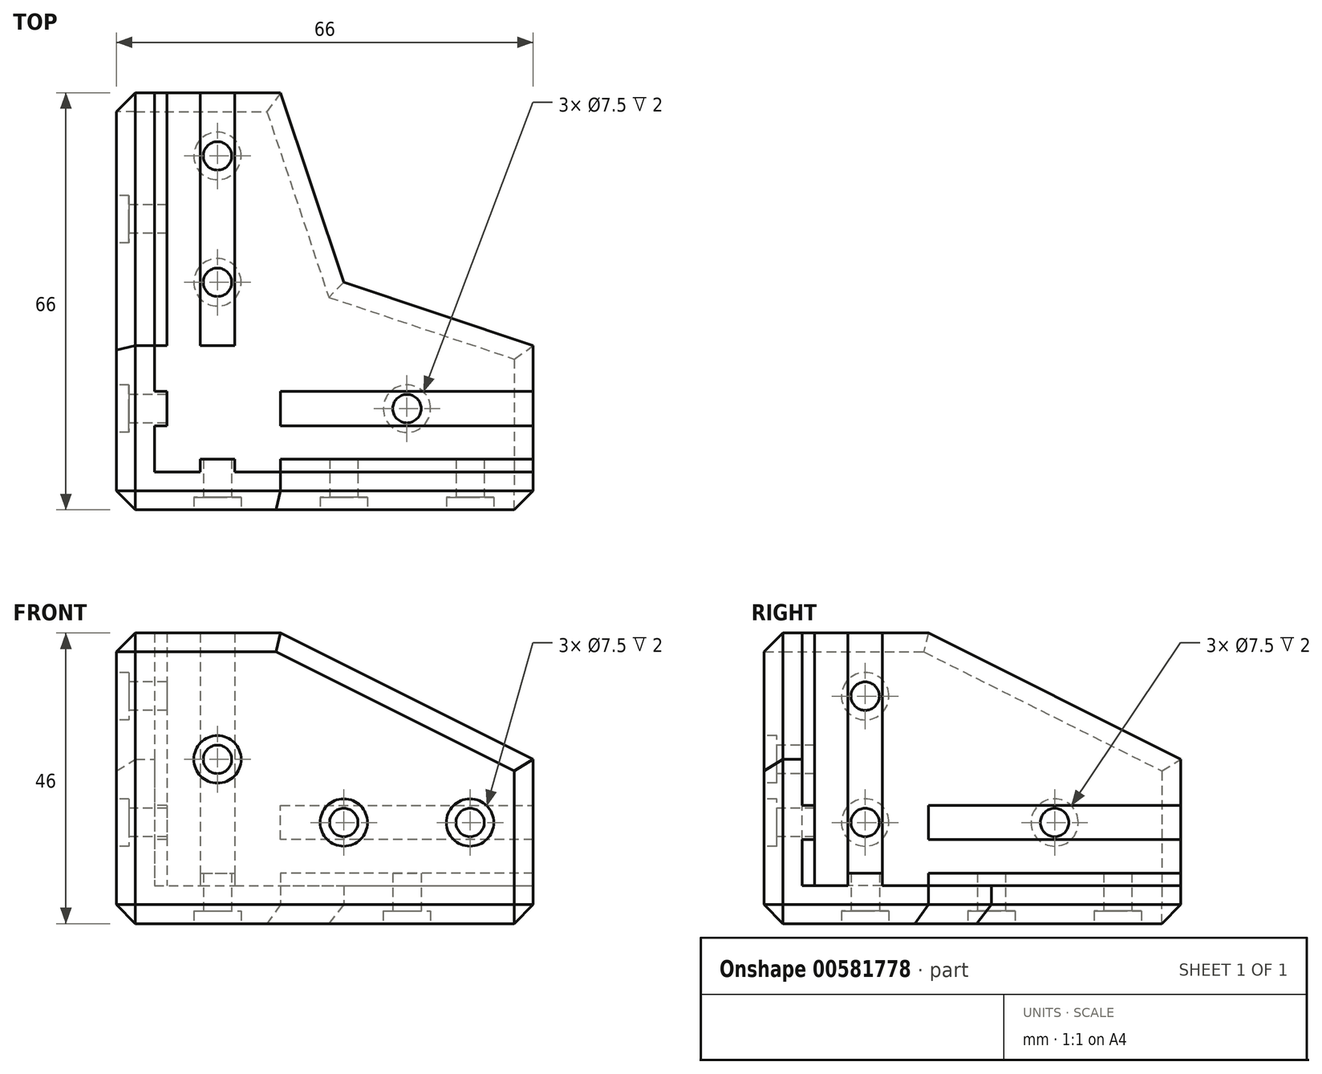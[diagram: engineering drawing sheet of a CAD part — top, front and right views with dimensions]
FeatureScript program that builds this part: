
annotation { "Feature Type Name" : "Feature", "Feature Type Description" : "" }
export const myFeature = defineFeature(function(context is Context, id is Id, definition is map)
    precondition{}
    {
        {
            var Q0;
            Q0=qCreatedBy(makeId("Top.planeOp"),FACE);
            var sketch = newSketch(context, id + "F0", { "sketchPlane" : qUnion([Q0])});
            skLineSegment(sketch, "E0", {"start": v(0, 0) * mm, "end": v(0, 66) * mm});
            skLineSegment(sketch, "E1", {"start": v(0, 66) * mm, "end": v(26, 66) * mm});
            skLineSegment(sketch, "E2", {"start": v(26, 66) * mm, "end": v(26, 26) * mm});
            skLineSegment(sketch, "E3", {"start": v(26, 26) * mm, "end": v(66, 26) * mm});
            skLineSegment(sketch, "E4", {"start": v(66, 26) * mm, "end": v(66, 0) * mm});
            skLineSegment(sketch, "E5", {"start": v(66, 0) * mm, "end": v(0, 0) * mm});
            skLineSegment(sketch, "E6", {"start": v(66, 6) * mm, "end": v(6, 6) * mm, "construction": true});
            skLineSegment(sketch, "E7", {"start": v(6, 6) * mm, "end": v(6, 66) * mm, "construction": true});
            skSolve(sketch);
        }
        {
            var Q0;
            Q0=qSketchRegion(id+"F0",true);
            extrude(context, id + "F1", {"entities" : qUnion([Q0]), "depth" : 6 * mm});
        }
        {
            var Q0;
            Q0=makeQuery(id+"F1.opExtrude","CAP_FACE",FACE,{"disambiguationData":[OSD([sQuery(id+"F0.wireOp",EDGE,"E0"),sQuery(id+"F0.wireOp",EDGE,"E1"),sQuery(id+"F0.wireOp",EDGE,"E2"),sQuery(id+"F0.wireOp",EDGE,"E3"),sQuery(id+"F0.wireOp",EDGE,"E4"),sQuery(id+"F0.wireOp",EDGE,"E5")])],"isStart":false});
            var sketch = newSketch(context, id + "F2", { "sketchPlane" : qUnion([Q0])});
            skLineSegment(sketch, "E8", {"start": v(0, 66) * mm, "end": v(6, 66) * mm});
            skLineSegment(sketch, "E9", {"start": v(6, 66) * mm, "end": v(6, 6) * mm});
            skLineSegment(sketch, "E10", {"start": v(6, 6) * mm, "end": v(66, 6) * mm});
            skLineSegment(sketch, "E11", {"start": v(66, 6) * mm, "end": v(66, 0) * mm});
            skLineSegment(sketch, "E12", {"start": v(66, 0) * mm, "end": v(0, 0) * mm});
            skLineSegment(sketch, "E13", {"start": v(0, 0) * mm, "end": v(0, 66) * mm});
            skSolve(sketch);
        }
        {
            var Q0;
            Q0=makeQuery(id+"F2.imprint","IMPRINT",FACE,{"disambiguationData":[TD([[makeQuery(id+"F2.imprint","IMPRINT",EDGE,{"derivedFrom":sQuery(id+"F2.wireOp",EDGE,"E8")}),-1.0]])]});
            extrude(context, id + "F3", {"entities" : qUnion([Q0]), "operationType" : NewBodyOperationType.ADD, "depth" : 20 * mm});
        }
        {
            var Q0;
            Q0=makeQuery(id+"F3.opExtrude","CAP_FACE",FACE,{"disambiguationData":[OSD([sQuery(id+"F2.wireOp",EDGE,"E8"),sQuery(id+"F2.wireOp",EDGE,"E9"),sQuery(id+"F2.wireOp",EDGE,"E10"),sQuery(id+"F2.wireOp",EDGE,"E11"),sQuery(id+"F2.wireOp",EDGE,"E12"),sQuery(id+"F2.wireOp",EDGE,"E13")])],"isStart":false});
            var sketch = newSketch(context, id + "F4", { "sketchPlane" : qUnion([Q0])});
            skLineSegment(sketch, "E14", {"start": v(6, 26) * mm, "end": v(0, 26) * mm});
            skLineSegment(sketch, "E15", {"start": v(0, 26) * mm, "end": v(0, 0) * mm});
            skLineSegment(sketch, "E16", {"start": v(0, 0) * mm, "end": v(26, 0) * mm});
            skLineSegment(sketch, "E17", {"start": v(26, 0) * mm, "end": v(26, 6) * mm});
            skLineSegment(sketch, "E18", {"start": v(26, 6) * mm, "end": v(6, 6) * mm});
            skLineSegment(sketch, "E19", {"start": v(6, 6) * mm, "end": v(6, 26) * mm});
            skSolve(sketch);
        }
        {
            var Q0;
            Q0=qSketchRegion(id+"F4",true);
            extrude(context, id + "F5", {"entities" : qUnion([Q0]), "operationType" : NewBodyOperationType.ADD, "depth" : 20 * mm});
        }
        {
            var Q0;
            Q0=makeQuery(id+"F1.opExtrude","CAP_FACE",FACE,{"disambiguationData":[OSD([sQuery(id+"F0.wireOp",EDGE,"E0"),sQuery(id+"F0.wireOp",EDGE,"E1"),sQuery(id+"F0.wireOp",EDGE,"E2"),sQuery(id+"F0.wireOp",EDGE,"E3"),sQuery(id+"F0.wireOp",EDGE,"E4"),sQuery(id+"F0.wireOp",EDGE,"E5")])],"isStart":false});
            var sketch = newSketch(context, id + "F6", { "sketchPlane" : qUnion([Q0])});
            skLineSegment(sketch, "E20", {"start": v(66, 16) * mm, "end": v(6, 16) * mm, "construction": true});
            skLineSegment(sketch, "E21", {"start": v(16, 66) * mm, "end": v(16, 6) * mm, "construction": true});
            skLineSegment(sketch, "E22", {"start": v(16, 6) * mm, "end": v(18.71, 6) * mm});
            skLineSegment(sketch, "E23", {"start": v(18.71, 6) * mm, "end": v(18.71, 8) * mm});
            skLineSegment(sketch, "E24", {"start": v(18.71, 8) * mm, "end": v(13.3, 8) * mm});
            skLineSegment(sketch, "E25", {"start": v(13.3, 8) * mm, "end": v(13.3, 6) * mm});
            skLineSegment(sketch, "E26", {"start": v(13.3, 6) * mm, "end": v(16, 6) * mm});
            skLineSegment(sketch, "E27", {"start": v(6, 16) * mm, "end": v(6, 18.7) * mm});
            skLineSegment(sketch, "E28", {"start": v(6, 18.7) * mm, "end": v(8, 18.7) * mm});
            skLineSegment(sketch, "E29", {"start": v(8, 18.7) * mm, "end": v(8, 13.29) * mm});
            skLineSegment(sketch, "E30", {"start": v(8, 13.29) * mm, "end": v(6, 13.29) * mm});
            skLineSegment(sketch, "E31", {"start": v(6, 13.29) * mm, "end": v(6, 16) * mm});
            skSolve(sketch);
        }
        {
            var Q0;
            Q0=qSketchRegion(id+"F6",true);
            extrude(context, id + "F7", {"entities" : qUnion([Q0]), "operationType" : NewBodyOperationType.ADD, "depth" : 40 * mm});
        }
        {
            var Q0;
            Q0=makeQuery(id+"F1.opExtrude","CAP_FACE",FACE,{"disambiguationData":[OSD([sQuery(id+"F0.wireOp",EDGE,"E0"),sQuery(id+"F0.wireOp",EDGE,"E1"),sQuery(id+"F0.wireOp",EDGE,"E2"),sQuery(id+"F0.wireOp",EDGE,"E3"),sQuery(id+"F0.wireOp",EDGE,"E4"),sQuery(id+"F0.wireOp",EDGE,"E5")])],"isStart":false});
            var sketch = newSketch(context, id + "F8", { "sketchPlane" : qUnion([Q0])});
            skLineSegment(sketch, "E32", {"start": v(66, 16) * mm, "end": v(8, 16) * mm, "construction": true});
            skLineSegment(sketch, "E33", {"start": v(66, 16) * mm, "end": v(66, 18.7) * mm});
            skLineSegment(sketch, "E34", {"start": v(66, 18.7) * mm, "end": v(26, 18.7) * mm});
            skLineSegment(sketch, "E35", {"start": v(26, 18.7) * mm, "end": v(26, 13.29) * mm});
            skLineSegment(sketch, "E36", {"start": v(26, 13.29) * mm, "end": v(66, 13.29) * mm});
            skLineSegment(sketch, "E37", {"start": v(66, 13.29) * mm, "end": v(66, 16) * mm});
            skLineSegment(sketch, "E38", {"start": v(16, 66) * mm, "end": v(16, 8) * mm, "construction": true});
            skLineSegment(sketch, "E39", {"start": v(16, 66) * mm, "end": v(13.3, 66) * mm});
            skLineSegment(sketch, "E40", {"start": v(13.3, 66) * mm, "end": v(13.3, 26) * mm});
            skLineSegment(sketch, "E41", {"start": v(13.3, 26) * mm, "end": v(18.7, 26) * mm});
            skLineSegment(sketch, "E42", {"start": v(18.7, 26) * mm, "end": v(18.7, 66) * mm});
            skLineSegment(sketch, "E43", {"start": v(18.7, 66) * mm, "end": v(16, 66) * mm});
            skSolve(sketch);
        }
        {
            var Q0;
            Q0=qSketchRegion(id+"F8",true);
            extrude(context, id + "F9", {"entities" : qUnion([Q0]), "operationType" : NewBodyOperationType.ADD, "depth" : 2 * mm});
        }
        {
            var Q0;
            {var subQ1=sQuery(id+"F2.wireOp",EDGE,"E10");var subQ2=sQuery(id+"F0.wireOp",EDGE,"E4");var subQ3=sQuery(id+"F4.wireOp",EDGE,"E18");Q0=makeQuery(id+"F7.boolean.opBoolean","SPLIT",FACE,{"disambiguationData":[TD([makeQuery(id+"F1.opExtrude","SWEPT_FACE",FACE,{"disambiguationData":[OSD([subQ2])]})])],"derivedFrom":makeQuery(id+"F5.boolean.opBoolean","MERGE",FACE,{"derivedFrom":[makeQuery(id+"F3.opExtrude","SWEPT_FACE",FACE,{"disambiguationData":[OSD([subQ1])]}),makeQuery(id+"F5.opExtrude","SWEPT_FACE",FACE,{"disambiguationData":[OSD([subQ3])]})]})});}
            var sketch = newSketch(context, id + "F10", { "sketchPlane" : qUnion([Q0])});
            skLineSegment(sketch, "E44", {"start": v(-66, 16) * mm, "end": v(-26, 16) * mm, "construction": true});
            skLineSegment(sketch, "E45", {"start": v(-66, 16) * mm, "end": v(-66, 13.3) * mm});
            skLineSegment(sketch, "E46", {"start": v(-66, 13.3) * mm, "end": v(-26, 13.3) * mm});
            skLineSegment(sketch, "E47", {"start": v(-26, 13.3) * mm, "end": v(-26, 16) * mm});
            skLineSegment(sketch, "E48", {"start": v(-26, 18.71) * mm, "end": v(-66, 18.71) * mm});
            skLineSegment(sketch, "E49", {"start": v(-66, 18.71) * mm, "end": v(-66, 16) * mm});
            skLineSegment(sketch, "E50", {"start": v(-26, 18.71) * mm, "end": v(-26, 16) * mm});
            skSolve(sketch);
        }
        {
            var Q0;
            Q0=qSketchRegion(id+"F10",true);
            extrude(context, id + "F11", {"entities" : qUnion([Q0]), "operationType" : NewBodyOperationType.ADD, "depth" : 2 * mm});
        }
        {
            var Q0;
            {var subQ0=sQuery(id+"F2.wireOp",EDGE,"E9");var subQ3=sQuery(id+"F0.wireOp",EDGE,"E1");var subQ5=sQuery(id+"F4.wireOp",EDGE,"E19");Q0=makeQuery(id+"F7.boolean.opBoolean","SPLIT",FACE,{"disambiguationData":[TD([makeQuery(id+"F1.opExtrude","SWEPT_FACE",FACE,{"disambiguationData":[OSD([subQ3])]})])],"derivedFrom":makeQuery(id+"F5.boolean.opBoolean","MERGE",FACE,{"derivedFrom":[makeQuery(id+"F3.opExtrude","SWEPT_FACE",FACE,{"disambiguationData":[OSD([subQ0])]}),makeQuery(id+"F5.opExtrude","SWEPT_FACE",FACE,{"disambiguationData":[OSD([subQ5])]})]})});}
            var sketch = newSketch(context, id + "F12", { "sketchPlane" : qUnion([Q0])});
            skLineSegment(sketch, "E51", {"start": v(66, 16) * mm, "end": v(26, 16) * mm, "construction": true});
            skLineSegment(sketch, "E52", {"start": v(66, 16) * mm, "end": v(66, 18.71) * mm});
            skLineSegment(sketch, "E53", {"start": v(66, 18.71) * mm, "end": v(26, 18.7) * mm});
            skLineSegment(sketch, "E54", {"start": v(26, 18.7) * mm, "end": v(26, 13.29) * mm});
            skLineSegment(sketch, "E55", {"start": v(26, 13.29) * mm, "end": v(66, 13.29) * mm});
            skLineSegment(sketch, "E56", {"start": v(66, 16) * mm, "end": v(66, 13.29) * mm});
            skSolve(sketch);
        }
        {
            var Q0;
            Q0=qSketchRegion(id+"F12",true);
            extrude(context, id + "F13", {"entities" : qUnion([Q0]), "operationType" : NewBodyOperationType.ADD, "depth" : 2 * mm});
        }
        {
            var Q0;
            Q0=makeQuery(id+"F5.boolean.opBoolean","MERGE",FACE,{"derivedFrom":[makeQuery(id+"F3.boolean.opBoolean","MERGE",FACE,{"derivedFrom":[makeQuery(id+"F1.opExtrude","SWEPT_FACE",FACE,{"disambiguationData":[OSD([sQuery(id+"F0.wireOp",EDGE,"E5")])]}),makeQuery(id+"F3.opExtrude","SWEPT_FACE",FACE,{"disambiguationData":[OSD([sQuery(id+"F2.wireOp",EDGE,"E12")])]})]}),makeQuery(id+"F5.opExtrude","SWEPT_FACE",FACE,{"disambiguationData":[OSD([sQuery(id+"F4.wireOp",EDGE,"E16")])]})]});
            var sketch = newSketch(context, id + "F14", { "sketchPlane" : qUnion([Q0])});
            skLineSegment(sketch, "E57", {"start": v(6, 46) * mm, "end": v(6, 6) * mm, "construction": true});
            skLineSegment(sketch, "E58", {"start": v(6, 6) * mm, "end": v(66, 6) * mm, "construction": true});
            skCircle(sketch, "E59", {"center": v(56, 16) * mm, "radius": 2.25 * mm});
            skCircle(sketch, "E60", {"center": v(36, 16) * mm, "radius": 2.25 * mm});
            skCircle(sketch, "E61", {"center": v(16, 26) * mm, "radius": 2.25 * mm});
            skLineSegment(sketch, "E62", {"start": v(26, 26) * mm, "end": v(6, 26) * mm, "construction": true});
            skLineSegment(sketch, "E63", {"start": v(26, 26) * mm, "end": v(26, 6) * mm, "construction": true});
            skSolve(sketch);
        }
        {
            var Q0;
            Q0=makeQuery(id+"F14.imprint","IMPRINT",FACE,{"disambiguationData":[TD([[makeQuery(id+"F14.imprint","IMPRINT",EDGE,{"derivedFrom":sQuery(id+"F14.wireOp",EDGE,"E59")}),1.0]])]});
            var Q1;
            Q1=makeQuery(id+"F14.imprint","IMPRINT",FACE,{"disambiguationData":[TD([[makeQuery(id+"F14.imprint","IMPRINT",EDGE,{"derivedFrom":sQuery(id+"F14.wireOp",EDGE,"E61")}),1.0]])]});
            var Q2;
            Q2=makeQuery(id+"F14.imprint","IMPRINT",FACE,{"disambiguationData":[TD([[makeQuery(id+"F14.imprint","IMPRINT",EDGE,{"derivedFrom":sQuery(id+"F14.wireOp",EDGE,"E60")}),1.0]])]});
            extrude(context, id + "F15", {"entities" : qUnion([Q0, Q1, Q2]), "operationType" : NewBodyOperationType.REMOVE, "endBound" : BoundingType.UP_TO_NEXT, "oppositeDirection" : true, "depth" : 25 * mm});
        }
        {
            var Q0;
            Q0=makeQuery(id+"F5.boolean.opBoolean","MERGE",FACE,{"derivedFrom":[makeQuery(id+"F3.boolean.opBoolean","MERGE",FACE,{"derivedFrom":[makeQuery(id+"F1.opExtrude","SWEPT_FACE",FACE,{"disambiguationData":[OSD([sQuery(id+"F0.wireOp",EDGE,"E0")])]}),makeQuery(id+"F3.opExtrude","SWEPT_FACE",FACE,{"disambiguationData":[OSD([sQuery(id+"F2.wireOp",EDGE,"E13")])]})]}),makeQuery(id+"F5.opExtrude","SWEPT_FACE",FACE,{"disambiguationData":[OSD([sQuery(id+"F4.wireOp",EDGE,"E15")])]})]});
            var sketch = newSketch(context, id + "F16", { "sketchPlane" : qUnion([Q0])});
            skLineSegment(sketch, "E64", {"start": v(-6, 46) * mm, "end": v(-6, 6) * mm, "construction": true});
            skLineSegment(sketch, "E65", {"start": v(-6, 6) * mm, "end": v(-66, 6) * mm, "construction": true});
            skCircle(sketch, "E66", {"center": v(-16, 36) * mm, "radius": 2.25 * mm});
            skCircle(sketch, "E67", {"center": v(-46, 16) * mm, "radius": 2.25 * mm});
            skCircle(sketch, "E68", {"center": v(-16, 16) * mm, "radius": 2.25 * mm});
            skSolve(sketch);
        }
        {
            var Q0;
            Q0=qSketchRegion(id+"F16",true);
            extrude(context, id + "F17", {"entities" : qUnion([Q0]), "operationType" : NewBodyOperationType.REMOVE, "endBound" : BoundingType.UP_TO_NEXT, "oppositeDirection" : true, "depth" : 25 * mm});
        }
        {
            var Q0;
            Q0=makeQuery(id+"F1.opExtrude","CAP_FACE",FACE,{"disambiguationData":[OSD([sQuery(id+"F0.wireOp",EDGE,"E0"),sQuery(id+"F0.wireOp",EDGE,"E1"),sQuery(id+"F0.wireOp",EDGE,"E2"),sQuery(id+"F0.wireOp",EDGE,"E3"),sQuery(id+"F0.wireOp",EDGE,"E4"),sQuery(id+"F0.wireOp",EDGE,"E5")])],"isStart":true});
            var sketch = newSketch(context, id + "F18", { "sketchPlane" : qUnion([Q0])});
            skLineSegment(sketch, "E69", {"start": v(66, -6) * mm, "end": v(6, -6) * mm, "construction": true});
            skLineSegment(sketch, "E70", {"start": v(6, -6) * mm, "end": v(6, -66) * mm, "construction": true});
            skCircle(sketch, "E71", {"center": v(46, -16) * mm, "radius": 2.25 * mm});
            skCircle(sketch, "E72", {"center": v(16, -56) * mm, "radius": 2.25 * mm});
            skCircle(sketch, "E73", {"center": v(16, -36) * mm, "radius": 2.25 * mm});
            skSolve(sketch);
        }
        {
            var Q0;
            Q0=qSketchRegion(id+"F18",true);
            extrude(context, id + "F19", {"entities" : qUnion([Q0]), "operationType" : NewBodyOperationType.REMOVE, "endBound" : BoundingType.UP_TO_NEXT, "oppositeDirection" : true, "depth" : 25 * mm});
        }
        {
            var Q0;
            Q0=makeQuery(id+"F5.boolean.opBoolean","MERGE",FACE,{"derivedFrom":[makeQuery(id+"F3.boolean.opBoolean","MERGE",FACE,{"derivedFrom":[makeQuery(id+"F1.opExtrude","SWEPT_FACE",FACE,{"disambiguationData":[OSD([sQuery(id+"F0.wireOp",EDGE,"E5")])]}),makeQuery(id+"F3.opExtrude","SWEPT_FACE",FACE,{"disambiguationData":[OSD([sQuery(id+"F2.wireOp",EDGE,"E12")])]})]}),makeQuery(id+"F5.opExtrude","SWEPT_FACE",FACE,{"disambiguationData":[OSD([sQuery(id+"F4.wireOp",EDGE,"E16")])]})]});
            var sketch = newSketch(context, id + "F20", { "sketchPlane" : qUnion([Q0])});
            skCircle(sketch, "E74", {"center": v(16, 26) * mm, "radius": 3.75 * mm});
            skCircle(sketch, "E75", {"center": v(36, 16) * mm, "radius": 3.75 * mm});
            skCircle(sketch, "E76", {"center": v(56, 16) * mm, "radius": 3.75 * mm});
            skSolve(sketch);
        }
        {
            var Q0;
            Q0=qSketchRegion(id+"F20",true);
            extrude(context, id + "F21", {"entities" : qUnion([Q0]), "operationType" : NewBodyOperationType.REMOVE, "oppositeDirection" : true, "depth" : 2 * mm});
        }
        {
            var Q0;
            Q0=makeQuery(id+"F5.boolean.opBoolean","MERGE",FACE,{"derivedFrom":[makeQuery(id+"F3.boolean.opBoolean","MERGE",FACE,{"derivedFrom":[makeQuery(id+"F1.opExtrude","SWEPT_FACE",FACE,{"disambiguationData":[OSD([sQuery(id+"F0.wireOp",EDGE,"E0")])]}),makeQuery(id+"F3.opExtrude","SWEPT_FACE",FACE,{"disambiguationData":[OSD([sQuery(id+"F2.wireOp",EDGE,"E13")])]})]}),makeQuery(id+"F5.opExtrude","SWEPT_FACE",FACE,{"disambiguationData":[OSD([sQuery(id+"F4.wireOp",EDGE,"E15")])]})]});
            var sketch = newSketch(context, id + "F22", { "sketchPlane" : qUnion([Q0])});
            skCircle(sketch, "E77", {"center": v(-16, 36) * mm, "radius": 3.75 * mm});
            skCircle(sketch, "E78", {"center": v(-46, 16) * mm, "radius": 3.75 * mm});
            skCircle(sketch, "E79", {"center": v(-16, 16) * mm, "radius": 3.75 * mm});
            skSolve(sketch);
        }
        {
            var Q0;
            Q0=qSketchRegion(id+"F22",true);
            extrude(context, id + "F23", {"entities" : qUnion([Q0]), "operationType" : NewBodyOperationType.REMOVE, "oppositeDirection" : true, "depth" : 2 * mm});
        }
        {
            var Q0;
            Q0=makeQuery(id+"F1.opExtrude","CAP_FACE",FACE,{"disambiguationData":[OSD([sQuery(id+"F0.wireOp",EDGE,"E0"),sQuery(id+"F0.wireOp",EDGE,"E1"),sQuery(id+"F0.wireOp",EDGE,"E2"),sQuery(id+"F0.wireOp",EDGE,"E3"),sQuery(id+"F0.wireOp",EDGE,"E4"),sQuery(id+"F0.wireOp",EDGE,"E5")])],"isStart":true});
            var sketch = newSketch(context, id + "F24", { "sketchPlane" : qUnion([Q0])});
            skCircle(sketch, "E80", {"center": v(16, -56) * mm, "radius": 3.75 * mm});
            skCircle(sketch, "E81", {"center": v(46, -16) * mm, "radius": 3.75 * mm});
            skCircle(sketch, "E82", {"center": v(16, -36) * mm, "radius": 3.75 * mm});
            skSolve(sketch);
        }
        {
            var Q0;
            Q0=qSketchRegion(id+"F24",true);
            extrude(context, id + "F25", {"entities" : qUnion([Q0]), "operationType" : NewBodyOperationType.REMOVE, "oppositeDirection" : true, "depth" : 2 * mm});
        }
        {
            var Q0;
            Q0=makeQuery(id+"F5.boolean.opBoolean","MERGE",FACE,{"derivedFrom":[makeQuery(id+"F3.boolean.opBoolean","MERGE",FACE,{"derivedFrom":[makeQuery(id+"F1.opExtrude","SWEPT_FACE",FACE,{"disambiguationData":[OSD([sQuery(id+"F0.wireOp",EDGE,"E5")])]}),makeQuery(id+"F3.opExtrude","SWEPT_FACE",FACE,{"disambiguationData":[OSD([sQuery(id+"F2.wireOp",EDGE,"E12")])]})]}),makeQuery(id+"F5.opExtrude","SWEPT_FACE",FACE,{"disambiguationData":[OSD([sQuery(id+"F4.wireOp",EDGE,"E16")])]})]});
            var sketch = newSketch(context, id + "F26", { "sketchPlane" : qUnion([Q0])});
            skLineSegment(sketch, "E83", {"start": v(26, 46) * mm, "end": v(26, 26) * mm});
            skLineSegment(sketch, "E84", {"start": v(26, 26) * mm, "end": v(66, 26) * mm});
            skLineSegment(sketch, "E85", {"start": v(66, 26) * mm, "end": v(26, 46) * mm});
            skSolve(sketch);
        }
        {
            var Q0;
            Q0=qSketchRegion(id+"F26",true);
            extrude(context, id + "F27", {"entities" : qUnion([Q0]), "operationType" : NewBodyOperationType.ADD, "oppositeDirection" : true, "depth" : 6 * mm});
        }
        {
            var Q0;
            Q0=makeQuery(id+"F5.boolean.opBoolean","MERGE",FACE,{"derivedFrom":[makeQuery(id+"F3.boolean.opBoolean","MERGE",FACE,{"derivedFrom":[makeQuery(id+"F1.opExtrude","SWEPT_FACE",FACE,{"disambiguationData":[OSD([sQuery(id+"F0.wireOp",EDGE,"E0")])]}),makeQuery(id+"F3.opExtrude","SWEPT_FACE",FACE,{"disambiguationData":[OSD([sQuery(id+"F2.wireOp",EDGE,"E13")])]})]}),makeQuery(id+"F5.opExtrude","SWEPT_FACE",FACE,{"disambiguationData":[OSD([sQuery(id+"F4.wireOp",EDGE,"E15")])]})]});
            var sketch = newSketch(context, id + "F28", { "sketchPlane" : qUnion([Q0])});
            skLineSegment(sketch, "E86", {"start": v(-66, 26) * mm, "end": v(-26, 26) * mm});
            skLineSegment(sketch, "E87", {"start": v(-26, 26) * mm, "end": v(-26, 46) * mm});
            skLineSegment(sketch, "E88", {"start": v(-26, 46) * mm, "end": v(-66, 26) * mm});
            skSolve(sketch);
        }
        {
            var Q0;
            Q0=qSketchRegion(id+"F28",true);
            extrude(context, id + "F29", {"entities" : qUnion([Q0]), "operationType" : NewBodyOperationType.ADD, "oppositeDirection" : true, "depth" : 6 * mm});
        }
        {
            var Q0;
            Q0=makeQuery(id+"F1.opExtrude","CAP_FACE",FACE,{"disambiguationData":[OSD([sQuery(id+"F0.wireOp",EDGE,"E0"),sQuery(id+"F0.wireOp",EDGE,"E1"),sQuery(id+"F0.wireOp",EDGE,"E2"),sQuery(id+"F0.wireOp",EDGE,"E3"),sQuery(id+"F0.wireOp",EDGE,"E4"),sQuery(id+"F0.wireOp",EDGE,"E5")])],"isStart":true});
            var sketch = newSketch(context, id + "F30", { "sketchPlane" : qUnion([Q0])});
            skLineSegment(sketch, "E89", {"start": v(26, -66) * mm, "end": v(26, -26) * mm});
            skLineSegment(sketch, "E90", {"start": v(26, -26) * mm, "end": v(66, -26) * mm});
            skLineSegment(sketch, "E91", {"start": v(26, -36) * mm, "end": v(36, -36) * mm, "construction": true});
            skLineSegment(sketch, "E92", {"start": v(36, -36) * mm, "end": v(36, -26) * mm, "construction": true});
            skLineSegment(sketch, "E93", {"start": v(26, -66) * mm, "end": v(36, -36) * mm});
            skLineSegment(sketch, "E94", {"start": v(36, -36) * mm, "end": v(66, -26) * mm});
            skSolve(sketch);
        }
        {
            var Q0;
            Q0=qSketchRegion(id+"F30",true);
            extrude(context, id + "F31", {"entities" : qUnion([Q0]), "operationType" : NewBodyOperationType.ADD, "oppositeDirection" : true, "depth" : 6 * mm});
        }
        {
            var Q0;
            Q0=makeQuery(id+"F27.opExtrude","CAP_EDGE",EDGE,{"disambiguationData":[OSD([sQuery(id+"F26.wireOp",EDGE,"E85")])],"isStart":true});
            var Q1;
            Q1=makeQuery(id+"F5.opExtrude","CAP_EDGE",EDGE,{"disambiguationData":[OSD([sQuery(id+"F4.wireOp",EDGE,"E16")])],"isStart":false});
            var Q2;
            Q2=makeQuery(id+"F5.opExtrude","CAP_EDGE",EDGE,{"disambiguationData":[OSD([sQuery(id+"F4.wireOp",EDGE,"E15")])],"isStart":false});
            var Q3;
            Q3=makeQuery(id+"F29.opExtrude","CAP_EDGE",EDGE,{"disambiguationData":[OSD([sQuery(id+"F28.wireOp",EDGE,"E88")])],"isStart":true});
            var Q4;
            Q4=makeQuery(id+"F31.opExtrude","CAP_EDGE",EDGE,{"disambiguationData":[OSD([sQuery(id+"F30.wireOp",EDGE,"E93")])],"isStart":true});
            var Q5;
            Q5=makeQuery(id+"F31.opExtrude","CAP_EDGE",EDGE,{"disambiguationData":[OSD([sQuery(id+"F30.wireOp",EDGE,"E94")])],"isStart":true});
            var Q6;
            Q6=makeQuery(id+"F1.opExtrude","CAP_EDGE",EDGE,{"disambiguationData":[OSD([sQuery(id+"F0.wireOp",EDGE,"E1")])],"isStart":true});
            var Q7;
            Q7=makeQuery(id+"F1.opExtrude","CAP_EDGE",EDGE,{"disambiguationData":[OSD([sQuery(id+"F0.wireOp",EDGE,"E4")])],"isStart":true});
            var Q8;
            Q8=makeQuery(id+"F3.boolean.opBoolean","MERGE",EDGE,{"derivedFrom":[makeQuery(id+"F1.opExtrude","SWEPT_EDGE",EDGE,{"disambiguationData":[OSD([sQuery(id+"F0.wireOp",EDGE,"E4"),sQuery(id+"F0.wireOp",EDGE,"E5")])]}),makeQuery(id+"F3.opExtrude","SWEPT_EDGE",EDGE,{"disambiguationData":[OSD([sQuery(id+"F2.wireOp",EDGE,"E11"),sQuery(id+"F2.wireOp",EDGE,"E12")])]})]});
            var Q9;
            Q9=makeQuery(id+"F3.boolean.opBoolean","MERGE",EDGE,{"derivedFrom":[makeQuery(id+"F1.opExtrude","SWEPT_EDGE",EDGE,{"disambiguationData":[OSD([sQuery(id+"F0.wireOp",EDGE,"E0"),sQuery(id+"F0.wireOp",EDGE,"E1")])]}),makeQuery(id+"F3.opExtrude","SWEPT_EDGE",EDGE,{"disambiguationData":[OSD([sQuery(id+"F2.wireOp",EDGE,"E8"),sQuery(id+"F2.wireOp",EDGE,"E13")])]})]});
            var Q10;
            Q10=makeQuery(id+"F1.opExtrude","CAP_EDGE",EDGE,{"disambiguationData":[OSD([sQuery(id+"F0.wireOp",EDGE,"E5")])],"isStart":true});
            var Q11;
            Q11=makeQuery(id+"F1.opExtrude","CAP_EDGE",EDGE,{"disambiguationData":[OSD([sQuery(id+"F0.wireOp",EDGE,"E0")])],"isStart":true});
            var Q12;
            Q12=makeQuery(id+"F5.boolean.opBoolean","MERGE",EDGE,{"derivedFrom":[makeQuery(id+"F3.boolean.opBoolean","MERGE",EDGE,{"derivedFrom":[makeQuery(id+"F1.opExtrude","SWEPT_EDGE",EDGE,{"disambiguationData":[OSD([sQuery(id+"F0.wireOp",EDGE,"E0"),sQuery(id+"F0.wireOp",EDGE,"E5")])]}),makeQuery(id+"F3.opExtrude","SWEPT_EDGE",EDGE,{"disambiguationData":[OSD([sQuery(id+"F2.wireOp",EDGE,"E12"),sQuery(id+"F2.wireOp",EDGE,"E13")])]})]}),makeQuery(id+"F5.opExtrude","SWEPT_EDGE",EDGE,{"disambiguationData":[OSD([sQuery(id+"F4.wireOp",EDGE,"E15"),sQuery(id+"F4.wireOp",EDGE,"E16")])]})]});
            chamfer(context, id + "F32", {"entities" : qUnion([Q0, Q1, Q2, Q3, Q4, Q5, Q6, Q7, Q8, Q9, Q10, Q11, Q12]), "width" : 3 * mm, "tangentPropagation" : true});
        }
    });
